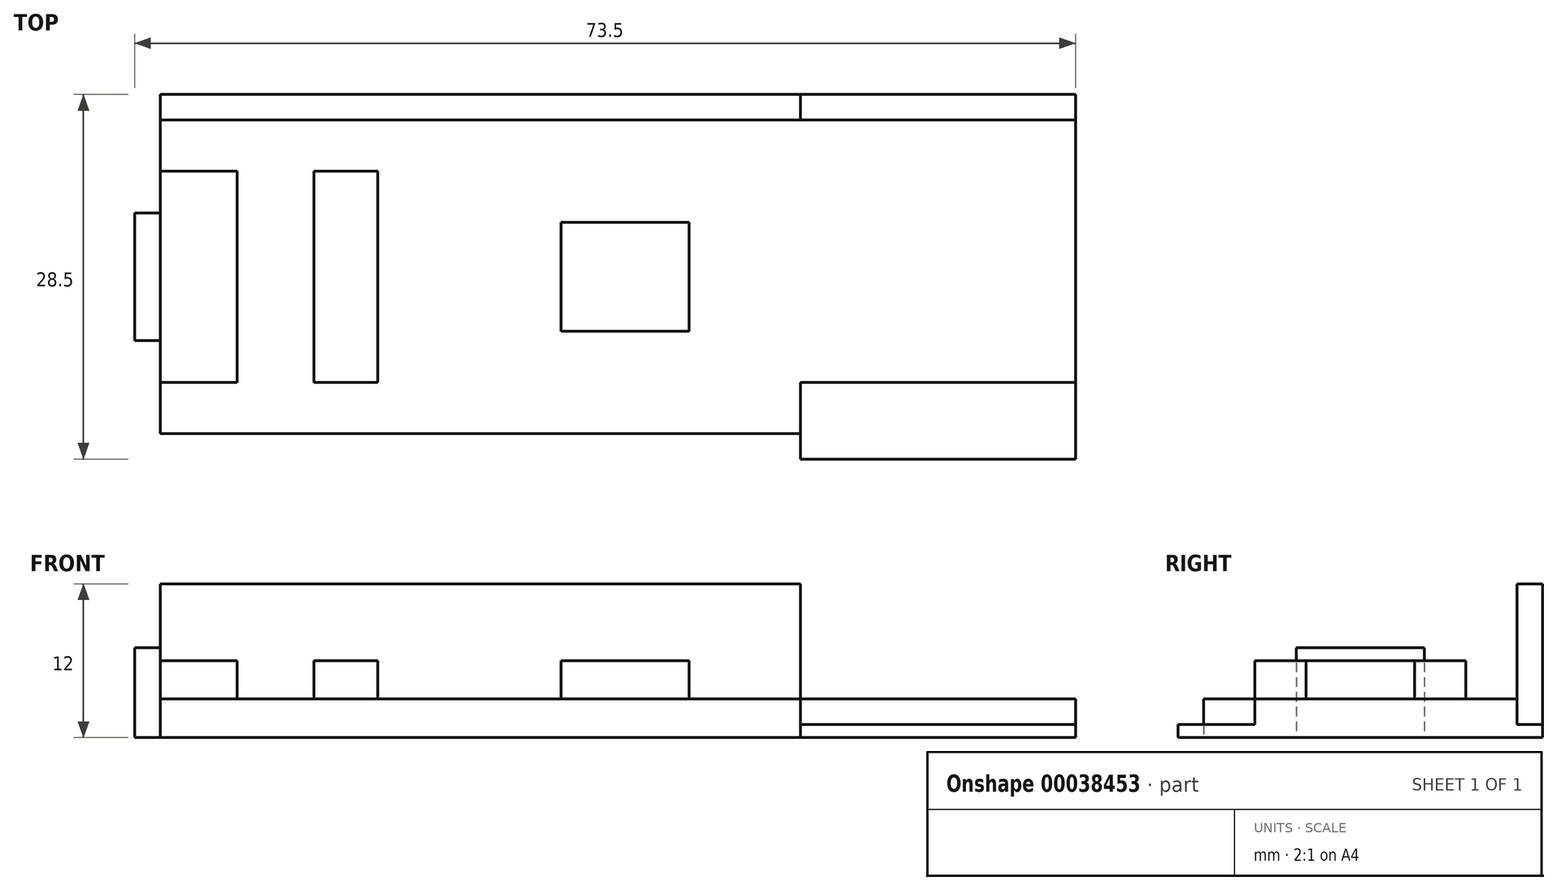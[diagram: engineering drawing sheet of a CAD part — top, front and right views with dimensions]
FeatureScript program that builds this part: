
annotation { "Feature Type Name" : "Feature", "Feature Type Description" : "" }
export const myFeature = defineFeature(function(context is Context, id is Id, definition is map)
    precondition{}
    {
        {
            var Q0;
            Q0=qCreatedBy(makeId("Top.planeOp"),FACE);
            var sketch = newSketch(context, id + "F0", { "sketchPlane" : qUnion([Q0])});
            skLineSegment(sketch, "E0.bottom", {"start": v(0, 0) * mm, "end": v(52, 0) * mm});
            skLineSegment(sketch, "E0.top", {"start": v(0, 28.5) * mm, "end": v(52, 28.5) * mm});
            skLineSegment(sketch, "E0.left", {"start": v(0, 0) * mm, "end": v(0, 28.5) * mm});
            skLineSegment(sketch, "E0.right", {"start": v(52, 0) * mm, "end": v(52, 28.5) * mm});
            skLineSegment(sketch, "E1.bottom", {"start": v(0, 28.5) * mm, "end": v(2, 28.5) * mm});
            skLineSegment(sketch, "E1.top", {"start": v(0, 0) * mm, "end": v(2, 0) * mm});
            skLineSegment(sketch, "E1.left", {"start": v(0, 28.5) * mm, "end": v(0, 0) * mm});
            skLineSegment(sketch, "E1.right", {"start": v(2, 28.5) * mm, "end": v(2, 0) * mm});
            skLineSegment(sketch, "E2.bottom", {"start": v(2, 26.5) * mm, "end": v(52, 26.5) * mm});
            skLineSegment(sketch, "E2.top", {"start": v(2, 28.5) * mm, "end": v(52, 28.5) * mm});
            skLineSegment(sketch, "E2.left", {"start": v(2, 26.5) * mm, "end": v(2, 28.5) * mm});
            skLineSegment(sketch, "E2.right", {"start": v(52, 26.5) * mm, "end": v(52, 28.5) * mm});
            skLineSegment(sketch, "E3.bottom", {"start": v(2, 0) * mm, "end": v(52, 0) * mm});
            skLineSegment(sketch, "E3.top", {"start": v(2, 2) * mm, "end": v(52, 2) * mm});
            skLineSegment(sketch, "E3.left", {"start": v(2, 0) * mm, "end": v(2, 2) * mm});
            skLineSegment(sketch, "E3.right", {"start": v(52, 0) * mm, "end": v(52, 2) * mm});
            skLineSegment(sketch, "E4", {"start": v(-6.31, 22.5) * mm, "end": v(72.94, 22.5) * mm, "construction": true});
            skLineSegment(sketch, "E5", {"start": v(-7.44, 6) * mm, "end": v(76.56, 6) * mm, "construction": true});
            skLineSegment(sketch, "E6.bottom", {"start": v(52, 26.5) * mm, "end": v(71, 26.5) * mm});
            skLineSegment(sketch, "E6.top", {"start": v(52, 6) * mm, "end": v(71, 6) * mm});
            skLineSegment(sketch, "E6.right", {"start": v(71, 26.5) * mm, "end": v(71, 6) * mm});
            skLineSegment(sketch, "E7.bottom", {"start": v(2, 22.5) * mm, "end": v(8, 22.5) * mm});
            skLineSegment(sketch, "E7.top", {"start": v(2, 6) * mm, "end": v(8, 6) * mm});
            skLineSegment(sketch, "E7.left", {"start": v(2, 22.5) * mm, "end": v(2, 6) * mm});
            skLineSegment(sketch, "E7.right", {"start": v(8, 22.5) * mm, "end": v(8, 6) * mm});
            skLineSegment(sketch, "E8.bottom", {"start": v(14, 22.5) * mm, "end": v(19, 22.5) * mm});
            skLineSegment(sketch, "E8.top", {"start": v(14, 6) * mm, "end": v(19, 6) * mm});
            skLineSegment(sketch, "E8.left", {"start": v(14, 22.5) * mm, "end": v(14, 6) * mm});
            skLineSegment(sketch, "E8.right", {"start": v(19, 22.5) * mm, "end": v(19, 6) * mm});
            skLineSegment(sketch, "E9.bottom", {"start": v(33.3, 18.5) * mm, "end": v(43.3, 18.5) * mm});
            skLineSegment(sketch, "E9.top", {"start": v(33.3, 10) * mm, "end": v(43.3, 10) * mm});
            skLineSegment(sketch, "E9.left", {"start": v(33.3, 18.5) * mm, "end": v(33.3, 10) * mm});
            skLineSegment(sketch, "E9.right", {"start": v(43.3, 18.5) * mm, "end": v(43.3, 10) * mm});
            skLineSegment(sketch, "E10.bottom", {"start": v(0, 19.25) * mm, "end": v(2, 19.25) * mm});
            skLineSegment(sketch, "E10.top", {"start": v(0, 9.25) * mm, "end": v(2, 9.25) * mm});
            skLineSegment(sketch, "E10.left", {"start": v(0, 19.25) * mm, "end": v(0, 9.25) * mm});
            skLineSegment(sketch, "E10.right", {"start": v(2, 19.25) * mm, "end": v(2, 9.25) * mm});
            skLineSegment(sketch, "E11", {"start": v(2, 14.25) * mm, "end": v(0, 14.25) * mm, "construction": true});
            skPoint(sketch, "E11.endSnap0", {"position": v(2, 14.25) * mm});
            skPoint(sketch, "E12.oppositeSnap0", {"position": v(71, 16.25) * mm});
            skLineSegment(sketch, "E12.left", {"start": v(52, 28.5) * mm, "end": v(52, 0) * mm});
            skLineSegment(sketch, "E13.bottom", {"start": v(52, 28.5) * mm, "end": v(73.5, 28.5) * mm});
            skLineSegment(sketch, "E13.top", {"start": v(52, 0) * mm, "end": v(73.5, 0) * mm});
            skLineSegment(sketch, "E13.right", {"start": v(73.5, 28.5) * mm, "end": v(73.5, 0) * mm});
            skLineSegment(sketch, "E14", {"start": v(71, 26.5) * mm, "end": v(73.5, 26.5) * mm});
            skLineSegment(sketch, "E15", {"start": v(71, 6) * mm, "end": v(73.5, 6) * mm});
            skSolve(sketch);
        }
        {
            var Q0;
            {var subQ0=sQuery(id+"F0.wireOp",EDGE,"E6.bottom");Q0=makeQuery(id+"F0.imprint","IMPRINT",FACE,{"disambiguationData":[TD([[makeQuery(id+"F0.imprint","IMPRINT",EDGE,{"derivedFrom":subQ0}),-1.0]])]});}
            var Q1;
            {var subQ7=sQuery(id+"F0.wireOp",EDGE,"E2.bottom");Q1=makeQuery(id+"F0.imprint","IMPRINT",FACE,{"disambiguationData":[TD([[makeQuery(id+"F0.imprint","IMPRINT",EDGE,{"derivedFrom":subQ7}),-1.0]])]});}
            var Q2;
            Q2=makeQuery(id+"F0.imprint","IMPRINT",FACE,{"disambiguationData":[TD([[makeQuery(id+"F0.imprint","IMPRINT",EDGE,{"derivedFrom":sQuery(id+"F0.wireOp",EDGE,"E6.right")}),1.0]])]});
            extrude(context, id + "F1", {"entities" : qUnion([Q0, Q1, Q2]), "depth" : 3 * mm});
        }
        {
            var Q0;
            {var subQ4=sQuery(id+"F0.wireOp",EDGE,"E7.bottom");Q0=makeQuery(id+"F0.imprint","IMPRINT",FACE,{"disambiguationData":[TD([[makeQuery(id+"F0.imprint","IMPRINT",EDGE,{"derivedFrom":subQ4}),-1.0]])]});}
            var Q1;
            Q1=makeQuery(id+"F0.imprint","IMPRINT",FACE,{"disambiguationData":[TD([[makeQuery(id+"F0.imprint","IMPRINT",EDGE,{"derivedFrom":sQuery(id+"F0.wireOp",EDGE,"E8.bottom")}),-1.0]])]});
            var Q2;
            Q2=makeQuery(id+"F0.imprint","IMPRINT",FACE,{"disambiguationData":[TD([[makeQuery(id+"F0.imprint","IMPRINT",EDGE,{"derivedFrom":sQuery(id+"F0.wireOp",EDGE,"E9.bottom")}),-1.0]])]});
            extrude(context, id + "F2", {"entities" : qUnion([Q0, Q1, Q2]), "operationType" : NewBodyOperationType.ADD, "depth" : 6 * mm});
        }
        {
            var Q0;
            Q0=makeQuery(id+"F0.imprint","IMPRINT",FACE,{"disambiguationData":[TD([[makeQuery(id+"F0.imprint","IMPRINT",EDGE,{"derivedFrom":sQuery(id+"F0.wireOp",EDGE,"E10.bottom")}),-1.0]])]});
            extrude(context, id + "F3", {"entities" : qUnion([Q0]), "operationType" : NewBodyOperationType.ADD, "depth" : 7 * mm});
        }
        {
            var Q0;
            Q0=makeQuery(id+"F0.imprint","IMPRINT",FACE,{"disambiguationData":[TD([[makeQuery(id+"F0.imprint","IMPRINT",EDGE,{"derivedFrom":sQuery(id+"F0.wireOp",EDGE,"E2.bottom")}),1.0]])]});
            var Q1;
            {var subQ5=sQuery(id+"F0.wireOp",EDGE,"E1.bottom");Q1=makeQuery(id+"F0.imprint","IMPRINT",FACE,{"disambiguationData":[TD([[makeQuery(id+"F0.imprint","IMPRINT",EDGE,{"derivedFrom":subQ5}),-1.0]])]});}
            var Q2;
            {var subQ5=sQuery(id+"F0.wireOp",EDGE,"E1.top");Q2=makeQuery(id+"F0.imprint","IMPRINT",FACE,{"disambiguationData":[TD([[makeQuery(id+"F0.imprint","IMPRINT",EDGE,{"derivedFrom":subQ5}),1.0]])]});}
            var Q3;
            Q3=makeQuery(id+"F0.imprint","IMPRINT",FACE,{"disambiguationData":[TD([[makeQuery(id+"F0.imprint","IMPRINT",EDGE,{"derivedFrom":sQuery(id+"F0.wireOp",EDGE,"E3.bottom")}),1.0]])]});
            extrude(context, id + "F4", {"entities" : qUnion([Q0, Q1, Q2, Q3]), "operationType" : NewBodyOperationType.ADD, "depth" : 12 * mm});
        }
        {
            var Q0;
            {var subQ5=sQuery(id+"F0.wireOp",EDGE,"E6.bottom");Q0=makeQuery(id+"F0.imprint","IMPRINT",FACE,{"disambiguationData":[TD([[makeQuery(id+"F0.imprint","IMPRINT",EDGE,{"derivedFrom":subQ5}),1.0]])]});}
            var Q1;
            {var subQ3=sQuery(id+"F0.wireOp",EDGE,"E6.top");Q1=makeQuery(id+"F0.imprint","IMPRINT",FACE,{"disambiguationData":[TD([[makeQuery(id+"F0.imprint","IMPRINT",EDGE,{"derivedFrom":subQ3}),-1.0]])]});}
            extrude(context, id + "F5", {"entities" : qUnion([Q0, Q1]), "operationType" : NewBodyOperationType.ADD, "depth" : 1 * mm});
        }
    });
